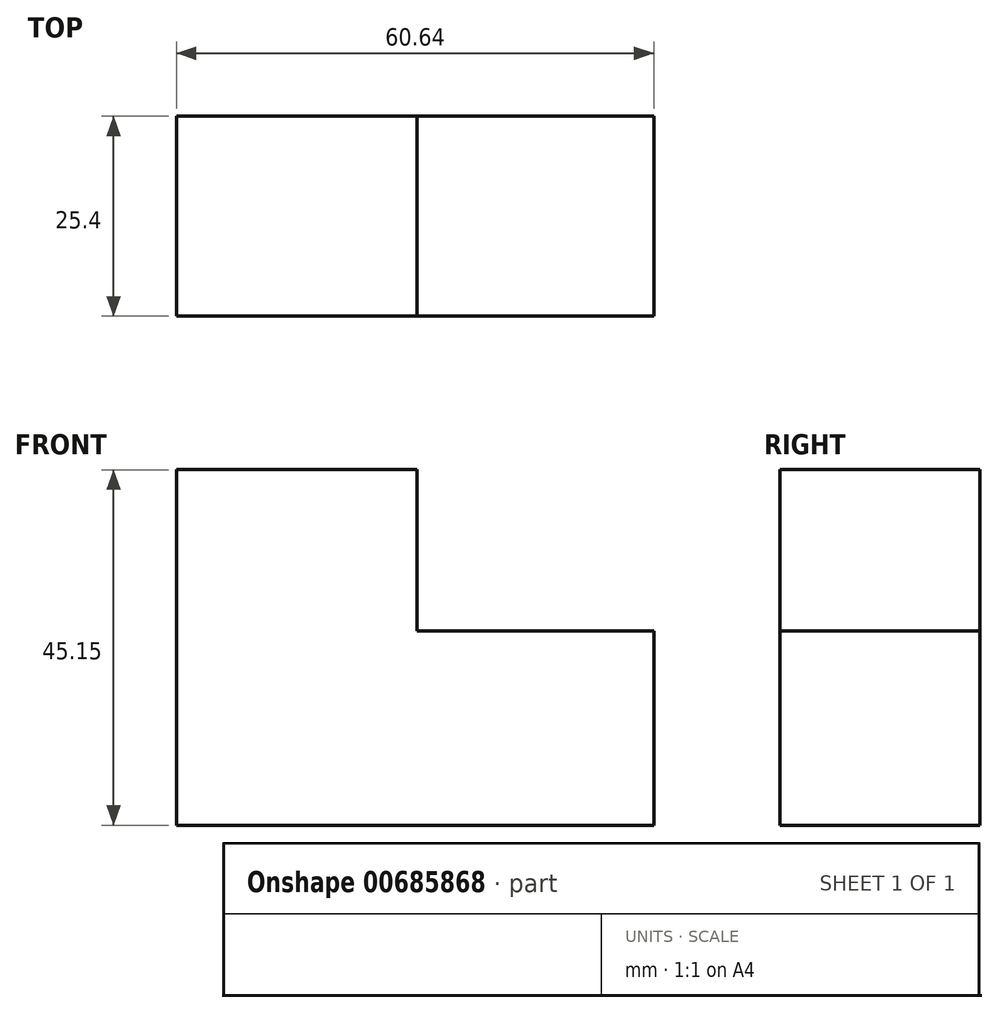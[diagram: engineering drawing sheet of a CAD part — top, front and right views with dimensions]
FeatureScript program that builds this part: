
annotation { "Feature Type Name" : "Feature", "Feature Type Description" : "" }
export const myFeature = defineFeature(function(context is Context, id is Id, definition is map)
    precondition{}
    {
        {
            var Q0;
            Q0=qCreatedBy(makeId("Front.planeOp"),FACE);
            var sketch = newSketch(context, id + "F0", { "sketchPlane" : qUnion([Q0])});
            skLineSegment(sketch, "E0", {"start": v(0, 0) * mm, "end": v(-60.64, 0) * mm});
            skLineSegment(sketch, "E1", {"start": v(-60.64, 0) * mm, "end": v(-60.64, 45.15) * mm});
            skLineSegment(sketch, "E2", {"start": v(-60.64, 45.15) * mm, "end": v(-30.06, 45.15) * mm});
            skLineSegment(sketch, "E3", {"start": v(-30.06, 45.15) * mm, "end": v(-30.06, 24.65) * mm});
            skPoint(sketch, "E4.start.orphan", {"position": v(0, 16.6) * mm});
            skLineSegment(sketch, "E5", {"start": v(-30.06, 24.65) * mm, "end": v(0, 24.65) * mm});
            skLineSegment(sketch, "E6", {"start": v(0, 24.65) * mm, "end": v(0, 0) * mm});
            skSolve(sketch);
        }
        {
            var Q0;
            Q0 = qSketchRegion(id + "F0", true);
            extrude(context, id + "F1", {"entities" : qUnion([Q0]), "depth" : 25.4 * mm, "offsetDistance" : 25.4 * mm});
        }
        {
            var Q0;
            Q0=makeQuery(id+"F0.imprint","IMPRINT",FACE,{"disambiguationData":[TD([[makeQuery(id+"F0.imprint","IMPRINT",EDGE,{"derivedFrom":sQuery(id+"F0.wireOp",EDGE,"E0")}),-1.0]])]});
            extrude(context, id + "F2", {"entities" : qUnion([Q0]), "operationType" : NewBodyOperationType.ADD, "depth" : 25.4 * mm, "offsetDistance" : 25.4 * mm});
        }
    });
